# Revit family: Access_Door_ACUDOR_Universal-Flush_UF-5000
name_source: partatom
category: Doors
revit_build: Autodesk Revit 2017 (Build: 20171027_0315(x64)
units: mm (PartAtom-declared; Revit-internal decimal feet)

## family parameters
Cut with Voids When Loaded = No
Host = Face
Room Calculation Point = No
Shared = No

## types (10) — shared parameters
Analytic Construction = <None>
Default Elevation = 48 "
Description = UNIVERSAL-FLUSH
Manufacturer = ACUDOR
Material Finish = Metal - Acudor - Stainless - Polished
URL = www.acudor.com
zero-valued in all types: Thickness, Wall Offset

## per-type parameters (varying)
| type | Code | Height | Width |
| UF-5000-1216 | 2 | 17.62 " | 13.62 " |
| UF-5000-0606 | 1 | 7.62 " | 7.62 " |
| UF-5000-0808 | 1 | 9.62 " | 9.62 " |
| UF-5000-0812 | 1 | 13.62 " | 9.62 " |
| UF-5000-1010 | 1 | 11.62 " | 11.62 " |
| UF-5000-1212 | 1 | 13.62 " | 13.62 " |
| UF-5000-1218 | 2 | 19.62 " | 13.62 " |
| UF-5000-1224 | 2 | 25.62 " | 13.62 " |
| UF-5000-1414 | 1 | 15.62 " | 15.62 " |
| UF-5000-1616 | 2 | 17.62 " | 17.62 " |

note: column(s) folded — value = type name in every type: Model

## geometry (parser evidence)
native form markers: Blend x2, Sweep x5
no freeform markers — native parametric forms only
